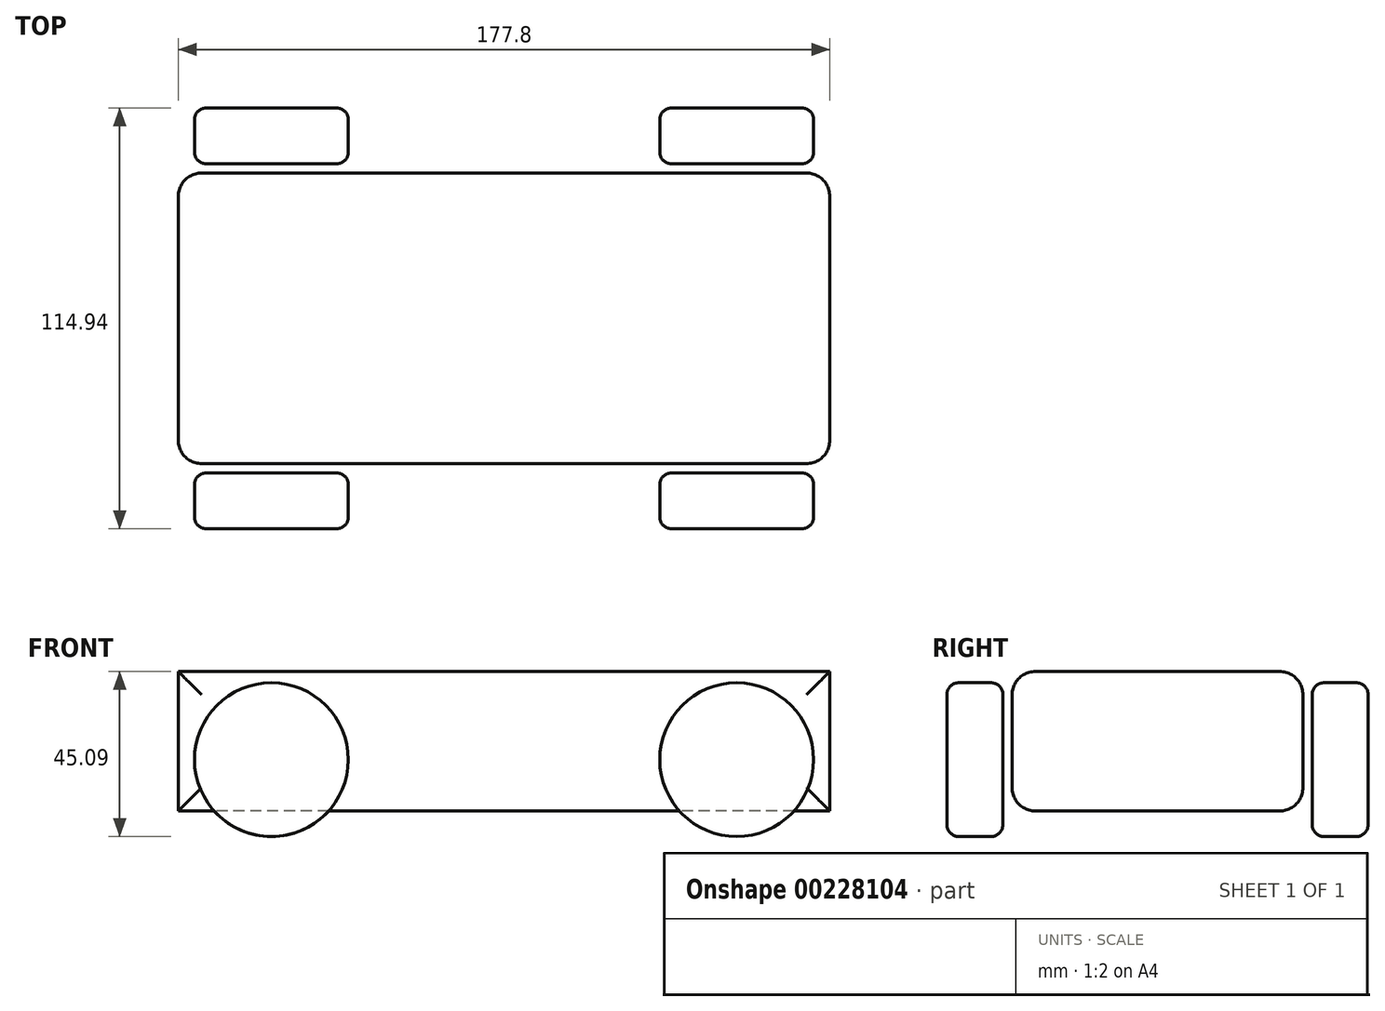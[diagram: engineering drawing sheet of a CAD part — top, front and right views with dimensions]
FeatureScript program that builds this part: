
annotation { "Feature Type Name" : "Feature", "Feature Type Description" : "" }
export const myFeature = defineFeature(function(context is Context, id is Id, definition is map)
    precondition{}
    {
        {
            var Q0;
            Q0=qCreatedBy(makeId("Front.planeOp"),FACE);
            var sketch = newSketch(context, id + "F0", { "sketchPlane" : qUnion([Q0])});
            skLineSegment(sketch, "E0.bottom", {"start": v(88.9, 19.05) * mm, "end": v(-88.9, 19.05) * mm});
            skLineSegment(sketch, "E0.top", {"start": v(88.9, -19.05) * mm, "end": v(-88.9, -19.05) * mm});
            skLineSegment(sketch, "E0.left", {"start": v(88.9, 19.05) * mm, "end": v(88.9, -19.05) * mm});
            skLineSegment(sketch, "E0.right", {"start": v(-88.9, 19.05) * mm, "end": v(-88.9, -19.05) * mm});
            skPoint(sketch, "E0.middle", {"position": v(0, 0) * mm});
            skLineSegment(sketch, "E1", {"start": v(-101.16, -26.04) * mm, "end": v(102.04, -26.03) * mm, "construction": true});
            skSolve(sketch);
        }
        {
            var Q0;
            Q0=qCreatedBy(makeId("Front.planeOp"),FACE);
            var sketch = newSketch(context, id + "F1", { "sketchPlane" : qUnion([Q0])});
            skLineSegment(sketch, "E2", {"start": v(-109.1, -26.04) * mm, "end": v(106.02, -26.03) * mm, "construction": true});
            skCircle(sketch, "E3", {"center": v(63.5, -5.03) * mm, "radius": 21 * mm});
            skSolve(sketch);
        }
        {
            var Q0;
            Q0 = qSketchRegion(id + "F0", true);
            extrude(context, id + "F2", {"entities" : qUnion([Q0]), "endBound" : BoundingType.SYMMETRIC, "depth" : 79.38 * mm});
        }
        {
            var Q0;
            Q0=makeQuery(id+"F2.opExtrude","CAP_FACE",FACE,{"disambiguationData":[OSD([sQuery(id+"F0.wireOp",EDGE,"E0.bottom"),sQuery(id+"F0.wireOp",EDGE,"E0.top"),sQuery(id+"F0.wireOp",EDGE,"E0.left"),sQuery(id+"F0.wireOp",EDGE,"E0.right")])],"isStart":false});
            cPlane(context, id + "F3", {"entities" : qUnion([Q0]), "cplaneType" : CPlaneType.OFFSET, "offset" : 2.54 * mm, "width" : 152.4 * mm, "height" : 152.4 * mm});
        }
        {
            var Q0;
            Q0=qCreatedBy(id+"F3.planeOp",FACE);
            var sketch = newSketch(context, id + "F4", { "sketchPlane" : qUnion([Q0])});
            skCircle(sketch, "E4.0", {"center": v(63.5, -5.03) * mm, "radius": 21 * mm});
            skSolve(sketch);
        }
        {
            var Q0;
            Q0 = qSketchRegion(id + "F4", true);
            extrude(context, id + "F5", {"entities" : qUnion([Q0]), "depth" : 15.24 * mm});
        }
        {
            var Q0;
            Q0=makeQuery(id+"F2.opExtrude","CAP_EDGE",EDGE,{"disambiguationData":[OSD([sQuery(id+"F0.wireOp",EDGE,"E0.bottom")])],"isStart":false});
            var Q1;
            Q1=makeQuery(id+"F2.opExtrude","CAP_EDGE",EDGE,{"disambiguationData":[OSD([sQuery(id+"F0.wireOp",EDGE,"E0.right")])],"isStart":false});
            var Q2;
            Q2=makeQuery(id+"F2.opExtrude","CAP_EDGE",EDGE,{"disambiguationData":[OSD([sQuery(id+"F0.wireOp",EDGE,"E0.top")])],"isStart":false});
            var Q3;
            Q3=makeQuery(id+"F2.opExtrude","CAP_EDGE",EDGE,{"disambiguationData":[OSD([sQuery(id+"F0.wireOp",EDGE,"E0.left")])],"isStart":false});
            var Q4;
            Q4=makeQuery(id+"F2.opExtrude","CAP_EDGE",EDGE,{"disambiguationData":[OSD([sQuery(id+"F0.wireOp",EDGE,"E0.left")])],"isStart":true});
            var Q5;
            Q5=makeQuery(id+"F2.opExtrude","CAP_EDGE",EDGE,{"disambiguationData":[OSD([sQuery(id+"F0.wireOp",EDGE,"E0.bottom")])],"isStart":true});
            var Q6;
            Q6=makeQuery(id+"F2.opExtrude","CAP_EDGE",EDGE,{"disambiguationData":[OSD([sQuery(id+"F0.wireOp",EDGE,"E0.right")])],"isStart":true});
            var Q7;
            Q7=makeQuery(id+"F2.opExtrude","CAP_EDGE",EDGE,{"disambiguationData":[OSD([sQuery(id+"F0.wireOp",EDGE,"E0.top")])],"isStart":true});
            fillet(context, id + "F6", {"entities" : qUnion([Q0, Q1, Q2, Q3, Q4, Q5, Q6, Q7]), "radius" : 6.35 * mm, "tangentPropagation" : true, "allowEdgeOverflow" : false});
        }
        {
            var Q0;
            Q0=makeQuery(id+"F5.opExtrude","CAP_FACE",FACE,{"disambiguationData":[OSD([sQuery(id+"F4.wireOp",EDGE,"E4.0")])],"isStart":false});
            var Q1;
            Q1=makeQuery(id+"F5.opExtrude","SWEPT_FACE",FACE,{"disambiguationData":[OSD([sQuery(id+"F4.wireOp",EDGE,"E4.0")])]});
            fillet(context, id + "F7", {"entities" : qUnion([Q0, Q1]), "radius" : 3.17 * mm, "tangentPropagation" : true, "allowEdgeOverflow" : false});
        }
        {
            var Q0;
            Q0=makeQuery(id+"F5.opExtrude","SWEPT_BODY",BODY,{"disambiguationData":[OSD([sQuery(id+"F4.wireOp",EDGE,"E4.0")])]});
            var Q1;
            Q1=qCreatedBy(makeId("Front.planeOp"),FACE);
            mirror(context, id + "F8", {"entities" : qUnion([Q0]), "mirrorPlane" : qUnion([Q1])});
        }
        {
            var Q0;
            Q0=makeQuery(id+"F5.opExtrude","SWEPT_BODY",BODY,{"disambiguationData":[OSD([sQuery(id+"F4.wireOp",EDGE,"E4.0")])]});
            var Q1;
            Q1=makeQuery(id+"F8.opPattern","COPY",BODY,{"derivedFrom":makeQuery(id+"F5.opExtrude","SWEPT_BODY",BODY,{"disambiguationData":[OSD([sQuery(id+"F4.wireOp",EDGE,"E4.0")])]}),"instanceName":"1"});
            var Q2;
            Q2=qCreatedBy(makeId("Right.planeOp"),FACE);
            mirror(context, id + "F9", {"entities" : qUnion([Q0, Q1]), "mirrorPlane" : qUnion([Q2])});
        }
    });
